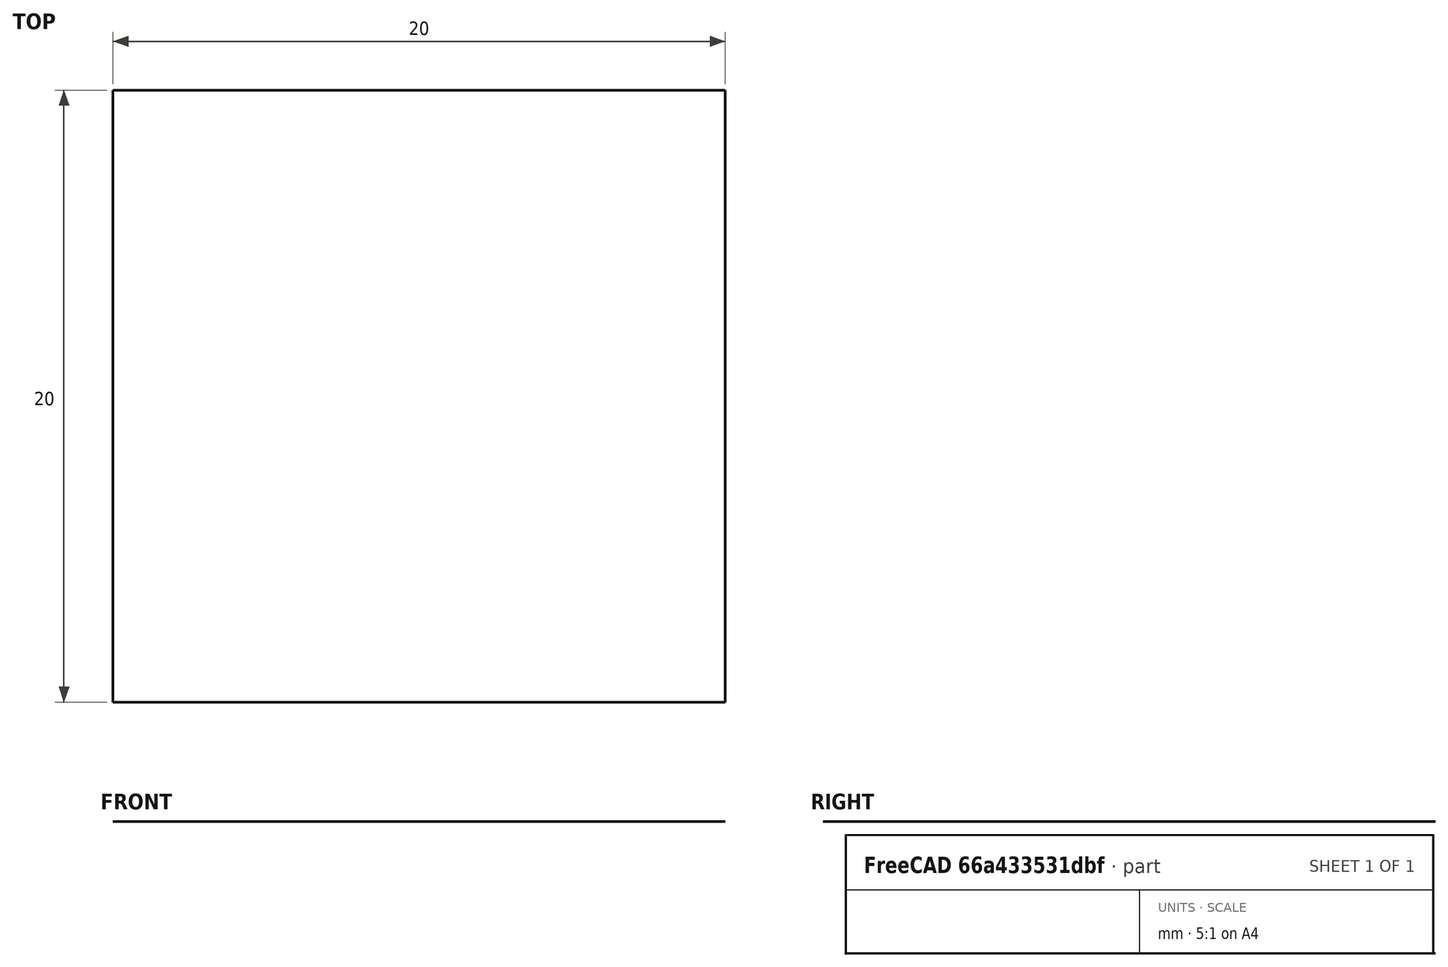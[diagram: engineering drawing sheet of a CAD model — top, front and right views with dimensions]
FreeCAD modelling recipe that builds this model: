
FCSTD DOCUMENT  (FreeCAD 0.16R6712 (Git))
Label: rule
License: All rights reserved
LicenseURL: http://en.wikipedia.org/wiki/All_rights_reserved
objects: Sketcher::SketchObject×1, Part::RuledSurface×1, Mesh::Feature×1
note: 2 computed .brp shape members not serialized (recipe doc carries the construction recipe); baked Part::Feature solids carry a one-line shape summary decoded from their .brp

FEATURE [Sketcher::SketchObject] Sketch
  sketch-geometry (4):
    g0: LineSegment StartX=-10 StartY=10 StartZ=0 EndX=10 EndY=10 EndZ=0
    g1: LineSegment StartX=10 StartY=-10 StartZ=0 EndX=-10 EndY=-10 EndZ=0
    g2: LineSegment StartX=-10 StartY=-10 StartZ=0 EndX=-10 EndY=10 EndZ=0
    g3: LineSegment StartX=10 StartY=10 StartZ=0 EndX=10 EndY=-10 EndZ=0
  constraints (11):
    c: Coincident(g1,g2)
    c: Coincident(g2,g0)
    c: Horizontal(g0)
    c: Horizontal(g1)
    c: Vertical(g2)
    c: Distance(g-1,g0) = 10
    c: Distance(g-1,g2) = 10
    c: Symmetric(g0,g0,g-2)
    c: Symmetric(g1,g1,g-2)
    c: Coincident(g3,g0)
    c: Coincident(g3,g1)
FEATURE [Part::RuledSurface] Ruled_Surface
  Curve1 = -> Sketch [Edge1]
  Curve2 = -> Sketch [Edge3]
  Orientation = 0
FEATURE [Mesh::Feature] Mesh  label="Ruled_Surface (Meshed)"
